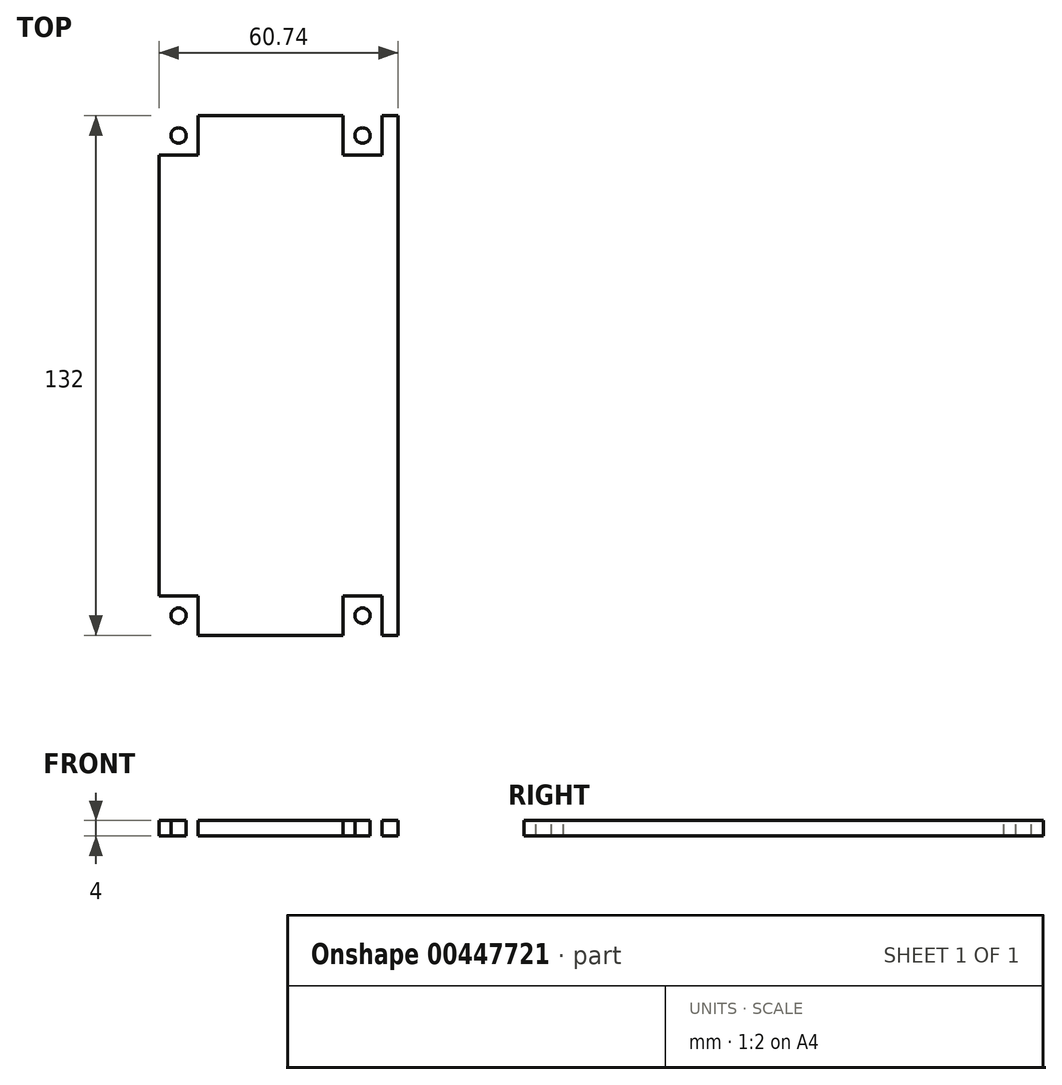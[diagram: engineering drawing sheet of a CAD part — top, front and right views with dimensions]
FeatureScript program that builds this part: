
annotation { "Feature Type Name" : "Feature", "Feature Type Description" : "" }
export const myFeature = defineFeature(function(context is Context, id is Id, definition is map)
    precondition{}
    {
        {
            var Q0;
            Q0=qCreatedBy(makeId("Top.planeOp"),FACE);
            var sketch = newSketch(context, id + "F0", { "sketchPlane" : qUnion([Q0])});
            skLineSegment(sketch, "E0.bottom", {"start": v(-30.37, 66) * mm, "end": v(30.37, 66) * mm});
            skLineSegment(sketch, "E0.top", {"start": v(-30.37, -66) * mm, "end": v(30.37, -66) * mm});
            skLineSegment(sketch, "E0.left", {"start": v(-30.37, 66) * mm, "end": v(-30.37, -66) * mm});
            skLineSegment(sketch, "E0.right", {"start": v(30.37, 66) * mm, "end": v(30.37, -66) * mm});
            skPoint(sketch, "E0.middle", {"position": v(0, 0) * mm});
            skSolve(sketch);
        }
        {
            var Q0;
            Q0=makeQuery(id+"F0.imprint","IMPRINT",FACE,{"disambiguationData":[TD([[makeQuery(id+"F0.imprint","IMPRINT",EDGE,{"derivedFrom":sQuery(id+"F0.wireOp",EDGE,"E0.bottom")}),-1.0]])]});
            extrude(context, id + "F1", {"entities" : qUnion([Q0]), "depth" : 4 * mm});
        }
        {
            var Q0;
            Q0=makeQuery(id+"F1.opExtrude","CAP_FACE",FACE,{"disambiguationData":[OSD([sQuery(id+"F0.wireOp",EDGE,"E0.bottom"),sQuery(id+"F0.wireOp",EDGE,"E0.top"),sQuery(id+"F0.wireOp",EDGE,"E0.left"),sQuery(id+"F0.wireOp",EDGE,"E0.right")])],"isStart":false});
            var sketch = newSketch(context, id + "F2", { "sketchPlane" : qUnion([Q0])});
            skLineSegment(sketch, "E1.bottom", {"start": v(-30.37, 66) * mm, "end": v(-20.37, 66) * mm});
            skLineSegment(sketch, "E1.top", {"start": v(-30.37, 56) * mm, "end": v(-20.37, 56) * mm});
            skLineSegment(sketch, "E1.left", {"start": v(-30.37, 66) * mm, "end": v(-30.37, 56) * mm});
            skLineSegment(sketch, "E1.right", {"start": v(-20.37, 66) * mm, "end": v(-20.37, 56) * mm});
            skLineSegment(sketch, "E2.bottom", {"start": v(-30.37, -66) * mm, "end": v(-20.37, -66) * mm});
            skLineSegment(sketch, "E2.top", {"start": v(-30.37, -56) * mm, "end": v(-20.37, -56) * mm});
            skLineSegment(sketch, "E2.left", {"start": v(-30.37, -66) * mm, "end": v(-30.37, -56) * mm});
            skLineSegment(sketch, "E2.right", {"start": v(-20.37, -66) * mm, "end": v(-20.37, -56) * mm});
            skLineSegment(sketch, "E3.bottom", {"start": v(30.37, 66) * mm, "end": v(26.37, 66) * mm});
            skLineSegment(sketch, "E3.top", {"start": v(30.37, 56) * mm, "end": v(26.37, 56) * mm});
            skLineSegment(sketch, "E3.left", {"start": v(30.37, 66) * mm, "end": v(30.37, 56) * mm});
            skLineSegment(sketch, "E3.right", {"start": v(26.37, 66) * mm, "end": v(26.37, 56) * mm});
            skLineSegment(sketch, "E4.bottom", {"start": v(30.37, -66) * mm, "end": v(26.37, -66) * mm});
            skLineSegment(sketch, "E4.top", {"start": v(30.37, -56) * mm, "end": v(26.37, -56) * mm});
            skLineSegment(sketch, "E4.left", {"start": v(30.37, -66) * mm, "end": v(30.37, -56) * mm});
            skLineSegment(sketch, "E4.right", {"start": v(26.37, -66) * mm, "end": v(26.37, -56) * mm});
            skLineSegment(sketch, "E5.bottom", {"start": v(26.37, 66) * mm, "end": v(16.37, 66) * mm});
            skLineSegment(sketch, "E5.top", {"start": v(26.37, 56) * mm, "end": v(16.37, 56) * mm});
            skLineSegment(sketch, "E5.right", {"start": v(16.37, 66) * mm, "end": v(16.37, 56) * mm});
            skLineSegment(sketch, "E6.bottom", {"start": v(26.37, -66) * mm, "end": v(16.37, -66) * mm});
            skLineSegment(sketch, "E6.top", {"start": v(26.37, -56) * mm, "end": v(16.37, -56) * mm});
            skLineSegment(sketch, "E6.right", {"start": v(16.37, -66) * mm, "end": v(16.37, -56) * mm});
            skLineSegment(sketch, "E7", {"start": v(-20.37, 56) * mm, "end": v(-30.37, 66) * mm});
            skLineSegment(sketch, "E8", {"start": v(-30.37, -56) * mm, "end": v(-20.37, -66) * mm});
            skLineSegment(sketch, "E9", {"start": v(16.37, 66) * mm, "end": v(26.37, 56) * mm});
            skLineSegment(sketch, "E10", {"start": v(16.37, -56) * mm, "end": v(26.37, -66) * mm});
            skCircle(sketch, "E11", {"center": v(-25.37, 61) * mm, "radius": 1.95 * mm});
            skCircle(sketch, "E12", {"center": v(21.37, 61) * mm, "radius": 1.95 * mm});
            skCircle(sketch, "E13", {"center": v(-25.37, -61) * mm, "radius": 1.95 * mm});
            skCircle(sketch, "E14", {"center": v(21.37, -61) * mm, "radius": 1.95 * mm});
            skSolve(sketch);
        }
        {
            var Q0;
            {var subQ0=sQuery(id+"F2.wireOp",EDGE,"E11");var subQ1=sQuery(id+"F2.wireOp",EDGE,"E7");var subQ2=makeQuery(id+"F2.imprint","INTERSECT",VERTEX,{"disambiguationData":[OD(0.0)],"derivedFrom":[subQ1,subQ0]});Q0=makeQuery(id+"F2.imprint","IMPRINT",FACE,{"disambiguationData":[TD([[makeQuery(id+"F2.imprint","IMPRINT",EDGE,{"disambiguationData":[TD([[subQ2,-1.0]])],"derivedFrom":subQ1}),1.0]])]});}
            var Q1;
            {var subQ0=sQuery(id+"F2.wireOp",EDGE,"E11");var subQ1=sQuery(id+"F2.wireOp",EDGE,"E7");var subQ2=makeQuery(id+"F2.imprint","INTERSECT",VERTEX,{"disambiguationData":[OD(0.0)],"derivedFrom":[subQ1,subQ0]});Q1=makeQuery(id+"F2.imprint","IMPRINT",FACE,{"disambiguationData":[TD([[makeQuery(id+"F2.imprint","IMPRINT",EDGE,{"disambiguationData":[TD([[subQ2,-1.0]])],"derivedFrom":subQ1}),-1.0]])]});}
            var Q2;
            {var subQ0=sQuery(id+"F2.wireOp",EDGE,"E12");var subQ1=sQuery(id+"F2.wireOp",EDGE,"E9");var subQ2=makeQuery(id+"F2.imprint","INTERSECT",VERTEX,{"disambiguationData":[OD(0.0)],"derivedFrom":[subQ1,subQ0]});Q2=makeQuery(id+"F2.imprint","IMPRINT",FACE,{"disambiguationData":[TD([[makeQuery(id+"F2.imprint","IMPRINT",EDGE,{"disambiguationData":[TD([[subQ2,-1.0]])],"derivedFrom":subQ1}),-1.0]])]});}
            var Q3;
            {var subQ0=sQuery(id+"F2.wireOp",EDGE,"E12");var subQ1=sQuery(id+"F2.wireOp",EDGE,"E9");var subQ2=makeQuery(id+"F2.imprint","INTERSECT",VERTEX,{"disambiguationData":[OD(0.0)],"derivedFrom":[subQ1,subQ0]});Q3=makeQuery(id+"F2.imprint","IMPRINT",FACE,{"disambiguationData":[TD([[makeQuery(id+"F2.imprint","IMPRINT",EDGE,{"disambiguationData":[TD([[subQ2,-1.0]])],"derivedFrom":subQ1}),1.0]])]});}
            var Q4;
            {var subQ0=sQuery(id+"F2.wireOp",EDGE,"E13");var subQ1=sQuery(id+"F2.wireOp",EDGE,"E8");var subQ2=makeQuery(id+"F2.imprint","INTERSECT",VERTEX,{"disambiguationData":[OD(0.0)],"derivedFrom":[subQ1,subQ0]});Q4=makeQuery(id+"F2.imprint","IMPRINT",FACE,{"disambiguationData":[TD([[makeQuery(id+"F2.imprint","IMPRINT",EDGE,{"disambiguationData":[TD([[subQ2,-1.0]])],"derivedFrom":subQ1}),1.0]])]});}
            var Q5;
            {var subQ0=sQuery(id+"F2.wireOp",EDGE,"E13");var subQ1=sQuery(id+"F2.wireOp",EDGE,"E8");var subQ2=makeQuery(id+"F2.imprint","INTERSECT",VERTEX,{"disambiguationData":[OD(0.0)],"derivedFrom":[subQ1,subQ0]});Q5=makeQuery(id+"F2.imprint","IMPRINT",FACE,{"disambiguationData":[TD([[makeQuery(id+"F2.imprint","IMPRINT",EDGE,{"disambiguationData":[TD([[subQ2,-1.0]])],"derivedFrom":subQ1}),-1.0]])]});}
            var Q6;
            {var subQ0=sQuery(id+"F2.wireOp",EDGE,"E14");var subQ1=sQuery(id+"F2.wireOp",EDGE,"E10");var subQ2=makeQuery(id+"F2.imprint","INTERSECT",VERTEX,{"disambiguationData":[OD(0.0)],"derivedFrom":[subQ1,subQ0]});Q6=makeQuery(id+"F2.imprint","IMPRINT",FACE,{"disambiguationData":[TD([[makeQuery(id+"F2.imprint","IMPRINT",EDGE,{"disambiguationData":[TD([[subQ2,-1.0]])],"derivedFrom":subQ1}),-1.0]])]});}
            var Q7;
            {var subQ0=sQuery(id+"F2.wireOp",EDGE,"E14");var subQ1=sQuery(id+"F2.wireOp",EDGE,"E10");var subQ2=makeQuery(id+"F2.imprint","INTERSECT",VERTEX,{"disambiguationData":[OD(0.0)],"derivedFrom":[subQ1,subQ0]});Q7=makeQuery(id+"F2.imprint","IMPRINT",FACE,{"disambiguationData":[TD([[makeQuery(id+"F2.imprint","IMPRINT",EDGE,{"disambiguationData":[TD([[subQ2,-1.0]])],"derivedFrom":subQ1}),1.0]])]});}
            extrude(context, id + "F3", {"entities" : qUnion([Q0, Q1, Q2, Q3, Q4, Q5, Q6, Q7]), "operationType" : NewBodyOperationType.REMOVE, "oppositeDirection" : true, "depth" : 4 * mm, "offsetDistance" : 25 * mm});
        }
    });
